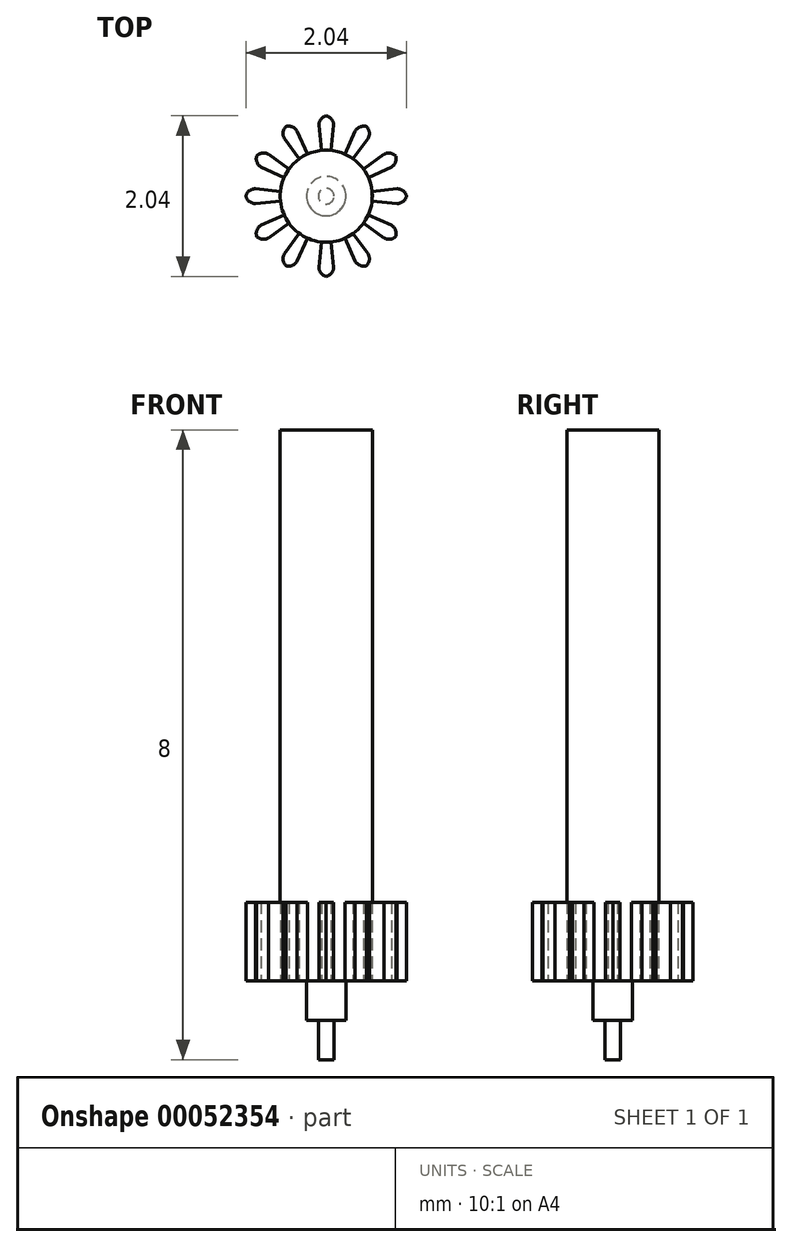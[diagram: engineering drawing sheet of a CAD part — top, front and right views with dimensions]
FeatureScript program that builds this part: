
annotation { "Feature Type Name" : "Feature", "Feature Type Description" : "" }
export const myFeature = defineFeature(function(context is Context, id is Id, definition is map)
    precondition{}
    {
        {
            var Q0;
            Q0=qCreatedBy(makeId("Top.planeOp"),FACE);
            var sketch = newSketch(context, id + "F0", { "sketchPlane" : qUnion([Q0])});
            skCircle(sketch, "E0", {"center": v(0, 0) * mm, "radius": 0.59 * mm, "construction": true});
            skCircle(sketch, "E1", {"center": v(0, 0) * mm, "radius": 0.9 * mm, "construction": true});
            skCircle(sketch, "E2", {"center": v(0, 0) * mm, "radius": 1.02 * mm, "construction": true});
            skLineSegment(sketch, "E3", {"start": v(0, 0.9) * mm, "end": v(0.1, 0.9) * mm, "construction": true});
            skLineSegment(sketch, "E4", {"start": v(0, 0.9) * mm, "end": v(-0.1, 0.9) * mm, "construction": true});
            skLineSegment(sketch, "E5", {"start": v(-0.1, 0.9) * mm, "end": v(0, 0) * mm, "construction": true});
            skLineSegment(sketch, "E6", {"start": v(0.1, 0.9) * mm, "end": v(0, 0) * mm, "construction": true});
            skLineSegment(sketch, "E7", {"start": v(-0.1, 0.9) * mm, "end": v(-0.06, 0.58) * mm});
            skLineSegment(sketch, "E8", {"start": v(0.1, 0.9) * mm, "end": v(0.06, 0.58) * mm});
            skCircle(sketch, "E9", {"center": v(-0.1, 0.9) * mm, "radius": 0.12 * mm, "construction": true});
            skCircle(sketch, "E10", {"center": v(0.1, 0.9) * mm, "radius": 0.12 * mm, "construction": true});
            skCircle(sketch, "E11", {"center": v(0, 1.02) * mm, "radius": 0.12 * mm, "construction": true});
            skArc(sketch, "E12", {"start": v(0.1, 0.9) * mm, "mid": v(0.07, 0.98) * mm, "end": v(0, 1.02) * mm});
            skArc(sketch, "E13", {"start": v(-0.1, 0.9) * mm, "mid": v(-0.07, 0.98) * mm, "end": v(0, 1.02) * mm});
            skCircle(sketch, "E14", {"center": v(0, 0) * mm, "radius": 0.59 * mm});
            skSolve(sketch);
        }
        {
            var Q0;
            {var subQ0=sQuery(id+"F0.wireOp",EDGE,"E7");Q0=makeQuery(id+"F0.imprint","IMPRINT",FACE,{"disambiguationData":[TD([[makeQuery(id+"F0.imprint","IMPRINT",EDGE,{"derivedFrom":subQ0}),1.0]])]});}
            extrude(context, id + "F1", {"entities" : qUnion([Q0]), "depth" : 1 * mm});
        }
        {
            var Q0;
            Q0=makeQuery(id+"F1.opExtrude","SWEPT_BODY",BODY,{"disambiguationData":[OSD([sQuery(id+"F0.wireOp",EDGE,"E7"),sQuery(id+"F0.wireOp",EDGE,"E8"),sQuery(id+"F0.wireOp",EDGE,"E12"),sQuery(id+"F0.wireOp",EDGE,"E13"),sQuery(id+"F0.wireOp",EDGE,"E14")])]});
            var Q1;
            Q1=makeQuery(id+"F1.opExtrude","CAP_EDGE",EDGE,{"disambiguationData":[OSD([sQuery(id+"F0.wireOp",EDGE,"E14")])],"isStart":false});
            circularPattern(context, id + "F2", {"entities" : qUnion([Q0]), "axis" : qUnion([Q1]), "angle" : 30 * degree, "instanceCount" : round(12)});
        }
        {
            var Q0;
            {var subQ0=sQuery(id+"F0.wireOp",EDGE,"E14");var subQ2=makeQuery(id+"F0.imprint","INTERSECT",VERTEX,{"derivedFrom":[sQuery(id+"F0.wireOp",EDGE,"E7"),subQ0]});Q0=makeQuery(id+"F0.imprint","IMPRINT",FACE,{"disambiguationData":[TD([[makeQuery(id+"F0.imprint","IMPRINT",EDGE,{"disambiguationData":[TD([[subQ2,1.0]])],"derivedFrom":subQ0}),1.0]])]});}
            extrude(context, id + "F3", {"entities" : qUnion([Q0]), "depth" : 7 * mm});
        }
        {
            var Q0;
            Q0=makeQuery(id+"F1.opExtrude","SWEPT_BODY",BODY,{"disambiguationData":[OSD([sQuery(id+"F0.wireOp",EDGE,"E7"),sQuery(id+"F0.wireOp",EDGE,"E8"),sQuery(id+"F0.wireOp",EDGE,"E12"),sQuery(id+"F0.wireOp",EDGE,"E13"),sQuery(id+"F0.wireOp",EDGE,"E14")])]});
            var Q1;
            Q1=makeQuery(id+"F2.opPattern","COPY",BODY,{"derivedFrom":makeQuery(id+"F1.opExtrude","SWEPT_BODY",BODY,{"disambiguationData":[OSD([sQuery(id+"F0.wireOp",EDGE,"E7"),sQuery(id+"F0.wireOp",EDGE,"E8"),sQuery(id+"F0.wireOp",EDGE,"E12"),sQuery(id+"F0.wireOp",EDGE,"E13"),sQuery(id+"F0.wireOp",EDGE,"E14")])]}),"instanceName":"6"});
            var Q2;
            Q2=makeQuery(id+"F2.opPattern","COPY",BODY,{"derivedFrom":makeQuery(id+"F1.opExtrude","SWEPT_BODY",BODY,{"disambiguationData":[OSD([sQuery(id+"F0.wireOp",EDGE,"E7"),sQuery(id+"F0.wireOp",EDGE,"E8"),sQuery(id+"F0.wireOp",EDGE,"E12"),sQuery(id+"F0.wireOp",EDGE,"E13"),sQuery(id+"F0.wireOp",EDGE,"E14")])]}),"instanceName":"11"});
            var Q3;
            Q3=makeQuery(id+"F2.opPattern","COPY",BODY,{"derivedFrom":makeQuery(id+"F1.opExtrude","SWEPT_BODY",BODY,{"disambiguationData":[OSD([sQuery(id+"F0.wireOp",EDGE,"E7"),sQuery(id+"F0.wireOp",EDGE,"E8"),sQuery(id+"F0.wireOp",EDGE,"E12"),sQuery(id+"F0.wireOp",EDGE,"E13"),sQuery(id+"F0.wireOp",EDGE,"E14")])]}),"instanceName":"9"});
            var Q4;
            Q4=makeQuery(id+"F2.opPattern","COPY",BODY,{"derivedFrom":makeQuery(id+"F1.opExtrude","SWEPT_BODY",BODY,{"disambiguationData":[OSD([sQuery(id+"F0.wireOp",EDGE,"E7"),sQuery(id+"F0.wireOp",EDGE,"E8"),sQuery(id+"F0.wireOp",EDGE,"E12"),sQuery(id+"F0.wireOp",EDGE,"E13"),sQuery(id+"F0.wireOp",EDGE,"E14")])]}),"instanceName":"10"});
            var Q5;
            Q5=makeQuery(id+"F2.opPattern","COPY",BODY,{"derivedFrom":makeQuery(id+"F1.opExtrude","SWEPT_BODY",BODY,{"disambiguationData":[OSD([sQuery(id+"F0.wireOp",EDGE,"E7"),sQuery(id+"F0.wireOp",EDGE,"E8"),sQuery(id+"F0.wireOp",EDGE,"E12"),sQuery(id+"F0.wireOp",EDGE,"E13"),sQuery(id+"F0.wireOp",EDGE,"E14")])]}),"instanceName":"8"});
            var Q6;
            Q6=makeQuery(id+"F2.opPattern","COPY",BODY,{"derivedFrom":makeQuery(id+"F1.opExtrude","SWEPT_BODY",BODY,{"disambiguationData":[OSD([sQuery(id+"F0.wireOp",EDGE,"E7"),sQuery(id+"F0.wireOp",EDGE,"E8"),sQuery(id+"F0.wireOp",EDGE,"E12"),sQuery(id+"F0.wireOp",EDGE,"E13"),sQuery(id+"F0.wireOp",EDGE,"E14")])]}),"instanceName":"5"});
            var Q7;
            Q7=makeQuery(id+"F2.opPattern","COPY",BODY,{"derivedFrom":makeQuery(id+"F1.opExtrude","SWEPT_BODY",BODY,{"disambiguationData":[OSD([sQuery(id+"F0.wireOp",EDGE,"E7"),sQuery(id+"F0.wireOp",EDGE,"E8"),sQuery(id+"F0.wireOp",EDGE,"E12"),sQuery(id+"F0.wireOp",EDGE,"E13"),sQuery(id+"F0.wireOp",EDGE,"E14")])]}),"instanceName":"3"});
            var Q8;
            Q8=makeQuery(id+"F2.opPattern","COPY",BODY,{"derivedFrom":makeQuery(id+"F1.opExtrude","SWEPT_BODY",BODY,{"disambiguationData":[OSD([sQuery(id+"F0.wireOp",EDGE,"E7"),sQuery(id+"F0.wireOp",EDGE,"E8"),sQuery(id+"F0.wireOp",EDGE,"E12"),sQuery(id+"F0.wireOp",EDGE,"E13"),sQuery(id+"F0.wireOp",EDGE,"E14")])]}),"instanceName":"7"});
            var Q9;
            Q9=makeQuery(id+"F2.opPattern","COPY",BODY,{"derivedFrom":makeQuery(id+"F1.opExtrude","SWEPT_BODY",BODY,{"disambiguationData":[OSD([sQuery(id+"F0.wireOp",EDGE,"E7"),sQuery(id+"F0.wireOp",EDGE,"E8"),sQuery(id+"F0.wireOp",EDGE,"E12"),sQuery(id+"F0.wireOp",EDGE,"E13"),sQuery(id+"F0.wireOp",EDGE,"E14")])]}),"instanceName":"1"});
            var Q10;
            Q10=makeQuery(id+"F2.opPattern","COPY",BODY,{"derivedFrom":makeQuery(id+"F1.opExtrude","SWEPT_BODY",BODY,{"disambiguationData":[OSD([sQuery(id+"F0.wireOp",EDGE,"E7"),sQuery(id+"F0.wireOp",EDGE,"E8"),sQuery(id+"F0.wireOp",EDGE,"E12"),sQuery(id+"F0.wireOp",EDGE,"E13"),sQuery(id+"F0.wireOp",EDGE,"E14")])]}),"instanceName":"2"});
            var Q11;
            Q11=makeQuery(id+"F2.opPattern","COPY",BODY,{"derivedFrom":makeQuery(id+"F1.opExtrude","SWEPT_BODY",BODY,{"disambiguationData":[OSD([sQuery(id+"F0.wireOp",EDGE,"E7"),sQuery(id+"F0.wireOp",EDGE,"E8"),sQuery(id+"F0.wireOp",EDGE,"E12"),sQuery(id+"F0.wireOp",EDGE,"E13"),sQuery(id+"F0.wireOp",EDGE,"E14")])]}),"instanceName":"4"});
            var Q12;
            Q12=makeQuery(id+"F3.opExtrude","SWEPT_BODY",BODY,{"disambiguationData":[OSD([sQuery(id+"F0.wireOp",EDGE,"E14")])]});
            booleanBodies(context, id + "F4", {"operationType" : BooleanOperationType.UNION, "tools" : qUnion([Q0, Q1, Q2, Q3, Q4, Q5, Q6, Q7, Q8, Q9, Q10, Q11, Q12])});
        }
        {
            var Q0;
            {var subQ0=sQuery(id+"F0.wireOp",EDGE,"E14");var subQ1=makeQuery(id+"F1.opExtrude","CAP_FACE",FACE,{"disambiguationData":[OSD([sQuery(id+"F0.wireOp",EDGE,"E7"),sQuery(id+"F0.wireOp",EDGE,"E8"),sQuery(id+"F0.wireOp",EDGE,"E12"),sQuery(id+"F0.wireOp",EDGE,"E13"),subQ0])],"isStart":true});Q0=makeQuery(id+"F4.opBoolean","MERGE",FACE,{"derivedFrom":[subQ1,makeQuery(id+"F2.opPattern","COPY",FACE,{"derivedFrom":subQ1,"instanceName":"1"}),makeQuery(id+"F2.opPattern","COPY",FACE,{"derivedFrom":subQ1,"instanceName":"2"}),makeQuery(id+"F2.opPattern","COPY",FACE,{"derivedFrom":subQ1,"instanceName":"3"}),makeQuery(id+"F2.opPattern","COPY",FACE,{"derivedFrom":subQ1,"instanceName":"4"}),makeQuery(id+"F2.opPattern","COPY",FACE,{"derivedFrom":subQ1,"instanceName":"5"}),makeQuery(id+"F2.opPattern","COPY",FACE,{"derivedFrom":subQ1,"instanceName":"6"}),makeQuery(id+"F2.opPattern","COPY",FACE,{"derivedFrom":subQ1,"instanceName":"7"}),makeQuery(id+"F2.opPattern","COPY",FACE,{"derivedFrom":subQ1,"instanceName":"8"}),makeQuery(id+"F2.opPattern","COPY",FACE,{"derivedFrom":subQ1,"instanceName":"9"}),makeQuery(id+"F2.opPattern","COPY",FACE,{"derivedFrom":subQ1,"instanceName":"10"}),makeQuery(id+"F2.opPattern","COPY",FACE,{"derivedFrom":subQ1,"instanceName":"11"}),makeQuery(id+"F3.opExtrude","CAP_FACE",FACE,{"disambiguationData":[OSD([subQ0])],"isStart":true})]});}
            var sketch = newSketch(context, id + "F5", { "sketchPlane" : qUnion([Q0])});
            skCircle(sketch, "E15", {"center": v(0, 0) * mm, "radius": 0.25 * mm});
            skSolve(sketch);
        }
        {
            var Q0;
            Q0=qSketchRegion(id+"F5",true);
            extrude(context, id + "F6", {"entities" : qUnion([Q0]), "operationType" : NewBodyOperationType.ADD, "depth" : 0.5 * mm});
        }
        {
            var Q0;
            Q0=makeQuery(id+"F6.opExtrude","CAP_FACE",FACE,{"disambiguationData":[OSD([sQuery(id+"F5.wireOp",EDGE,"E15")])],"isStart":false});
            var sketch = newSketch(context, id + "F7", { "sketchPlane" : qUnion([Q0])});
            skCircle(sketch, "E16", {"center": v(0, 0) * mm, "radius": 0.1 * mm});
            skSolve(sketch);
        }
        {
            var Q0;
            Q0=qSketchRegion(id+"F7",true);
            extrude(context, id + "F8", {"entities" : qUnion([Q0]), "operationType" : NewBodyOperationType.ADD, "depth" : 0.5 * mm});
        }
    });
